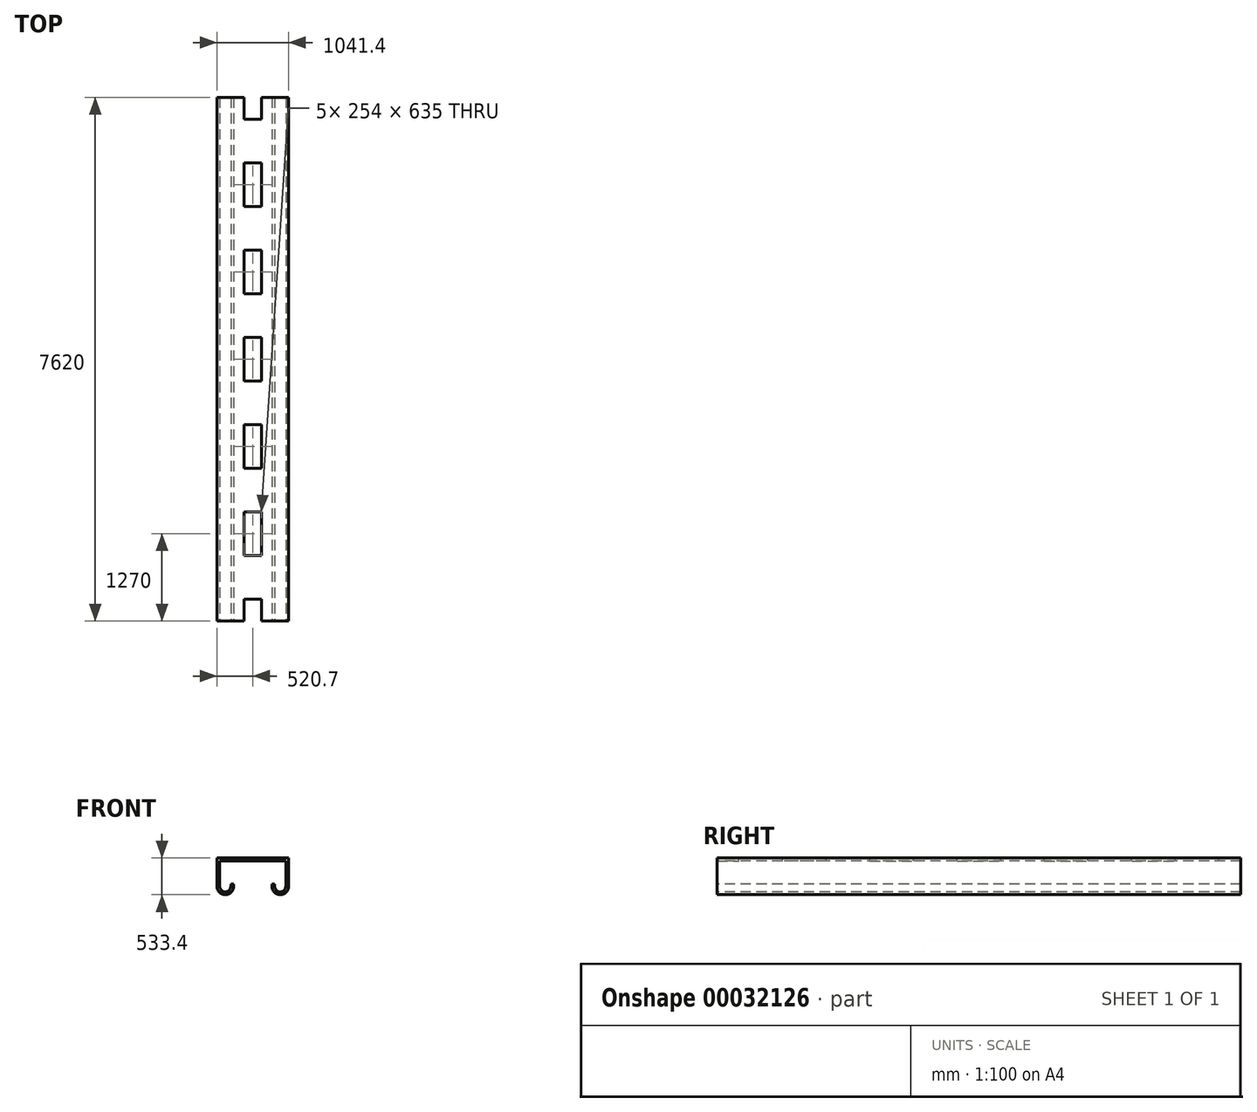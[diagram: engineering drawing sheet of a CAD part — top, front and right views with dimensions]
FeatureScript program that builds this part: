
annotation { "Feature Type Name" : "Feature", "Feature Type Description" : "" }
export const myFeature = defineFeature(function(context is Context, id is Id, definition is map)
    precondition{}
    {
        {
            var Q0;
            Q0=qCreatedBy(makeId("Front.planeOp"),FACE);
            var sketch = newSketch(context, id + "F0", { "sketchPlane" : qUnion([Q0])});
            skLineSegment(sketch, "E0", {"start": v(0, 0) * mm, "end": v(1041.4, 0) * mm});
            skLineSegment(sketch, "E1", {"start": v(1041.4, 0) * mm, "end": v(1041.4, -412.75) * mm});
            skLineSegment(sketch, "E2", {"start": v(0, 0) * mm, "end": v(0, -412.75) * mm});
            skArc(sketch, "E3", {"start": v(800.1, -412.75) * mm, "mid": v(920.75, -533.4) * mm, "end": v(1041.4, -412.75) * mm});
            skArc(sketch, "E4", {"start": v(0, -412.75) * mm, "mid": v(120.65, -533.4) * mm, "end": v(241.3, -412.75) * mm});
            skLineSegment(sketch, "E5", {"start": v(241.3, -412.75) * mm, "end": v(241.3, -381) * mm});
            skLineSegment(sketch, "E6", {"start": v(241.3, -381) * mm, "end": v(200.66, -381) * mm});
            skLineSegment(sketch, "E7", {"start": v(200.66, -381) * mm, "end": v(200.66, -412.75) * mm});
            skArc(sketch, "E8", {"start": v(40.64, -412.75) * mm, "mid": v(120.65, -492.76) * mm, "end": v(200.66, -412.75) * mm});
            skLineSegment(sketch, "E9", {"start": v(40.64, -412.75) * mm, "end": v(40.64, -40.64) * mm});
            skLineSegment(sketch, "E10", {"start": v(40.64, -40.64) * mm, "end": v(1000.76, -40.64) * mm});
            skLineSegment(sketch, "E11", {"start": v(1000.76, -40.64) * mm, "end": v(1000.76, -412.75) * mm});
            skArc(sketch, "E12", {"start": v(840.74, -412.75) * mm, "mid": v(920.75, -492.76) * mm, "end": v(1000.76, -412.75) * mm});
            skLineSegment(sketch, "E13", {"start": v(840.74, -412.75) * mm, "end": v(840.74, -381) * mm});
            skLineSegment(sketch, "E14", {"start": v(840.74, -381) * mm, "end": v(800.1, -381) * mm});
            skLineSegment(sketch, "E15", {"start": v(800.1, -381) * mm, "end": v(800.1, -412.75) * mm});
            skSolve(sketch);
        }
        {
            var Q0;
            Q0=qCreatedBy(makeId("Top.planeOp"),FACE);
            var sketch = newSketch(context, id + "F1", { "sketchPlane" : qUnion([Q0])});
            skLineSegment(sketch, "E16.bottom", {"start": v(0, 0) * mm, "end": v(1041.4, 0) * mm});
            skLineSegment(sketch, "E16.top", {"start": v(0, 7620) * mm, "end": v(1041.4, 7620) * mm});
            skLineSegment(sketch, "E16.left", {"start": v(0, 0) * mm, "end": v(0, 7620) * mm});
            skLineSegment(sketch, "E16.right", {"start": v(1041.4, 0) * mm, "end": v(1041.4, 7620) * mm});
            skPoint(sketch, "E17.0", {"position": v(1041.4, 0) * mm});
            skLineSegment(sketch, "E18.bottom", {"start": v(393.7, 1587.5) * mm, "end": v(647.7, 1587.5) * mm});
            skLineSegment(sketch, "E18.top", {"start": v(393.7, 952.5) * mm, "end": v(647.7, 952.5) * mm});
            skLineSegment(sketch, "E18.left", {"start": v(393.7, 1587.5) * mm, "end": v(393.7, 952.5) * mm});
            skLineSegment(sketch, "E18.right", {"start": v(647.7, 1587.5) * mm, "end": v(647.7, 952.5) * mm});
            skLineSegment(sketch, "E19", {"start": v(393.7, 0) * mm, "end": v(393.7, 317.5) * mm});
            skLineSegment(sketch, "E20", {"start": v(393.7, 317.5) * mm, "end": v(647.7, 317.5) * mm});
            skLineSegment(sketch, "E21", {"start": v(647.7, 317.5) * mm, "end": v(647.7, 0) * mm});
            skLineSegment(sketch, "E22", {"start": v(393.7, 7620) * mm, "end": v(393.7, 7302.5) * mm});
            skLineSegment(sketch, "E23", {"start": v(393.7, 7302.5) * mm, "end": v(647.7, 7302.5) * mm});
            skLineSegment(sketch, "E24", {"start": v(647.7, 7302.5) * mm, "end": v(647.7, 7620) * mm});
            skLineSegment(sketch, "E25.bottom", {"start": v(393.7, 2222.5) * mm, "end": v(647.7, 2222.5) * mm});
            skLineSegment(sketch, "E25.top", {"start": v(393.7, 2857.5) * mm, "end": v(647.7, 2857.5) * mm});
            skLineSegment(sketch, "E25.left", {"start": v(393.7, 2222.5) * mm, "end": v(393.7, 2857.5) * mm});
            skLineSegment(sketch, "E25.right", {"start": v(647.7, 2222.5) * mm, "end": v(647.7, 2857.5) * mm});
            skLineSegment(sketch, "E26.bottom", {"start": v(393.7, 3492.5) * mm, "end": v(647.7, 3492.5) * mm});
            skLineSegment(sketch, "E26.top", {"start": v(393.7, 4127.5) * mm, "end": v(647.7, 4127.5) * mm});
            skLineSegment(sketch, "E26.left", {"start": v(393.7, 3492.5) * mm, "end": v(393.7, 4127.5) * mm});
            skLineSegment(sketch, "E26.right", {"start": v(647.7, 3492.5) * mm, "end": v(647.7, 4127.5) * mm});
            skLineSegment(sketch, "E27.bottom", {"start": v(393.7, 4762.5) * mm, "end": v(647.7, 4762.5) * mm});
            skLineSegment(sketch, "E27.top", {"start": v(393.7, 5397.5) * mm, "end": v(647.7, 5397.5) * mm});
            skLineSegment(sketch, "E27.left", {"start": v(393.7, 4762.5) * mm, "end": v(393.7, 5397.5) * mm});
            skLineSegment(sketch, "E27.right", {"start": v(647.7, 4762.5) * mm, "end": v(647.7, 5397.5) * mm});
            skLineSegment(sketch, "E28.bottom", {"start": v(393.7, 6032.5) * mm, "end": v(647.7, 6032.5) * mm});
            skLineSegment(sketch, "E28.top", {"start": v(393.7, 6667.5) * mm, "end": v(647.7, 6667.5) * mm});
            skLineSegment(sketch, "E28.left", {"start": v(393.7, 6032.5) * mm, "end": v(393.7, 6667.5) * mm});
            skLineSegment(sketch, "E28.right", {"start": v(647.7, 6032.5) * mm, "end": v(647.7, 6667.5) * mm});
            skPoint(sketch, "E29", {"position": v(520.7, 317.5) * mm});
            skPoint(sketch, "E30", {"position": v(520.7, 0) * mm});
            skLineSegment(sketch, "E31", {"start": v(520.7, 1587.5) * mm, "end": v(520.7, 2222.5) * mm, "construction": true});
            skLineSegment(sketch, "E32", {"start": v(520.7, 2857.5) * mm, "end": v(520.7, 3492.5) * mm, "construction": true});
            skLineSegment(sketch, "E33", {"start": v(520.7, 4127.5) * mm, "end": v(520.7, 4762.5) * mm, "construction": true});
            skLineSegment(sketch, "E34", {"start": v(520.7, 5397.5) * mm, "end": v(520.7, 6032.5) * mm, "construction": true});
            skLineSegment(sketch, "E35", {"start": v(520.7, 952.5) * mm, "end": v(520.7, 317.5) * mm, "construction": true});
            skLineSegment(sketch, "E36", {"start": v(520.7, 7302.5) * mm, "end": v(520.7, 6667.5) * mm, "construction": true});
            skSolve(sketch);
        }
        {
            var Q0;
            Q0=makeQuery(id+"F0.imprint","IMPRINT",FACE,{"disambiguationData":[TD([[makeQuery(id+"F0.imprint","IMPRINT",EDGE,{"derivedFrom":sQuery(id+"F0.wireOp",EDGE,"E0")}),-1.0]])]});
            extrude(context, id + "F2", {"entities" : qUnion([Q0]), "oppositeDirection" : true, "depth" : 7620 * mm});
        }
        {
            var Q0;
            {var subQ1=sQuery(id+"F1.wireOp",EDGE,"E19");Q0=makeQuery(id+"F1.imprint","IMPRINT",FACE,{"disambiguationData":[TD([[makeQuery(id+"F1.imprint","IMPRINT",EDGE,{"derivedFrom":subQ1}),-1.0]])]});}
            var Q1;
            Q1=makeQuery(id+"F1.imprint","IMPRINT",FACE,{"disambiguationData":[TD([[makeQuery(id+"F1.imprint","IMPRINT",EDGE,{"derivedFrom":sQuery(id+"F1.wireOp",EDGE,"E18.bottom")}),-1.0]])]});
            var Q2;
            Q2=makeQuery(id+"F1.imprint","IMPRINT",FACE,{"disambiguationData":[TD([[makeQuery(id+"F1.imprint","IMPRINT",EDGE,{"derivedFrom":sQuery(id+"F1.wireOp",EDGE,"E25.bottom")}),1.0]])]});
            var Q3;
            Q3=makeQuery(id+"F1.imprint","IMPRINT",FACE,{"disambiguationData":[TD([[makeQuery(id+"F1.imprint","IMPRINT",EDGE,{"derivedFrom":sQuery(id+"F1.wireOp",EDGE,"E26.bottom")}),1.0]])]});
            var Q4;
            Q4=makeQuery(id+"F1.imprint","IMPRINT",FACE,{"disambiguationData":[TD([[makeQuery(id+"F1.imprint","IMPRINT",EDGE,{"derivedFrom":sQuery(id+"F1.wireOp",EDGE,"E27.bottom")}),1.0]])]});
            var Q5;
            Q5=makeQuery(id+"F1.imprint","IMPRINT",FACE,{"disambiguationData":[TD([[makeQuery(id+"F1.imprint","IMPRINT",EDGE,{"derivedFrom":sQuery(id+"F1.wireOp",EDGE,"E28.bottom")}),1.0]])]});
            var Q6;
            {var subQ1=sQuery(id+"F1.wireOp",EDGE,"E22");Q6=makeQuery(id+"F1.imprint","IMPRINT",FACE,{"disambiguationData":[TD([[makeQuery(id+"F1.imprint","IMPRINT",EDGE,{"derivedFrom":subQ1}),1.0]])]});}
            extrude(context, id + "F3", {"entities" : qUnion([Q0, Q1, Q2, Q3, Q4, Q5, Q6]), "operationType" : NewBodyOperationType.REMOVE, "oppositeDirection" : true, "depth" : 40.64 * mm});
        }
    });
